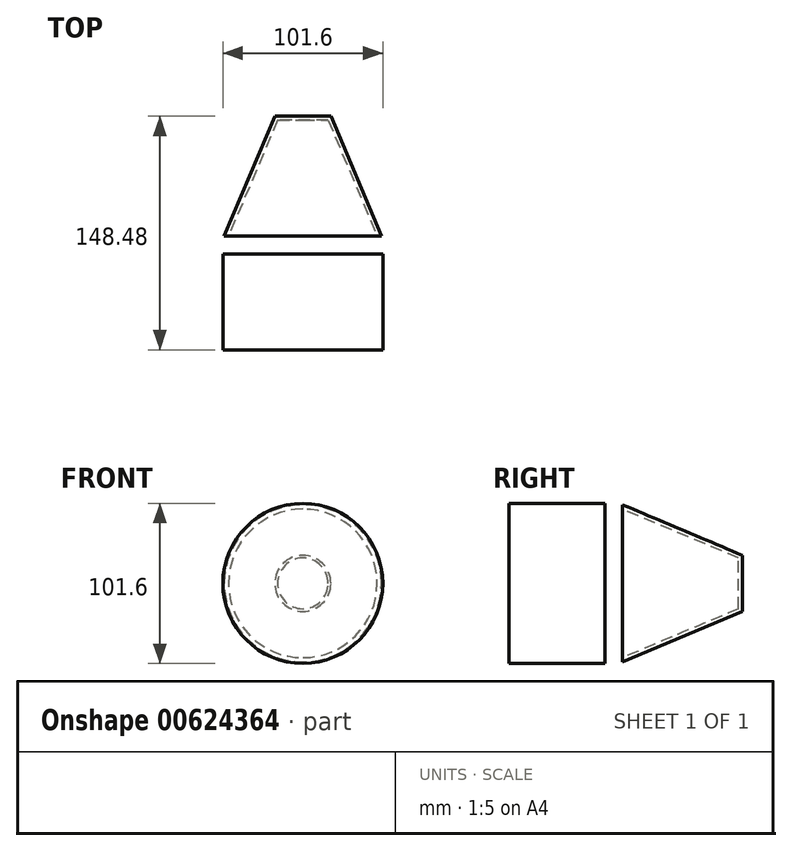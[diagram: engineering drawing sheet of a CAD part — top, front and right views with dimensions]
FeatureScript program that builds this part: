
annotation { "Feature Type Name" : "Feature", "Feature Type Description" : "" }
export const myFeature = defineFeature(function(context is Context, id is Id, definition is map)
    precondition{}
    {
        {
            var Q0;
            Q0=qCreatedBy(makeId("Front.planeOp"),FACE);
            var sketch = newSketch(context, id + "F0", { "sketchPlane" : qUnion([Q0])});
            skCircle(sketch, "E0", {"center": v(0, 0) * mm, "radius": 50.8 * mm});
            skSolve(sketch);
        }
        {
            var Q0;
            Q0=makeQuery(id+"F0.imprint","IMPRINT",FACE,{"disambiguationData":[TD([[makeQuery(id+"F0.imprint","IMPRINT",EDGE,{"derivedFrom":sQuery(id+"F0.wireOp",EDGE,"E0")}),1.0]])]});
            extrude(context, id + "F1", {"entities" : qUnion([Q0]), "oppositeDirection" : true, "depth" : 60.96 * mm, "offsetDistance" : 25.4 * mm});
        }
        {
            var Q0;
            Q0=qCreatedBy(makeId("Right.planeOp"),FACE);
            var sketch = newSketch(context, id + "F2", { "sketchPlane" : qUnion([Q0])});
            skLineSegment(sketch, "E1", {"start": v(72.28, 0) * mm, "end": v(72.28, 49.92) * mm});
            skLineSegment(sketch, "E2", {"start": v(72.28, 49.92) * mm, "end": v(148.48, 17.78) * mm});
            skLineSegment(sketch, "E3", {"start": v(148.48, 17.78) * mm, "end": v(148.48, 0) * mm});
            skLineSegment(sketch, "E4", {"start": v(148.48, 0) * mm, "end": v(72.28, 0) * mm});
            skSolve(sketch);
        }
        {
            var Q0;
            Q0=makeQuery(id+"F2.imprint","IMPRINT",FACE,{"disambiguationData":[TD([[makeQuery(id+"F2.imprint","IMPRINT",EDGE,{"derivedFrom":sQuery(id+"F2.wireOp",EDGE,"E1")}),-1.0]])]});
            var Q1;
            Q1=sQuery(id+"F2.wireOp",EDGE,"E4");
            revolve(context, id + "F3", {"entities" : qUnion([Q0]), "axis" : qUnion([Q1]), "revolveType" : RevolveType.FULL});
        }
        {
            var Q0;
            Q0=makeQuery(id+"F3.opRevolve","SWEPT_FACE",FACE,{"disambiguationData":[OSD([sQuery(id+"F2.wireOp",EDGE,"E1")])]});
            shell(context, id + "F4", {"entities" : qUnion([Q0]), "thickness" : 2.54 * mm});
        }
    });
